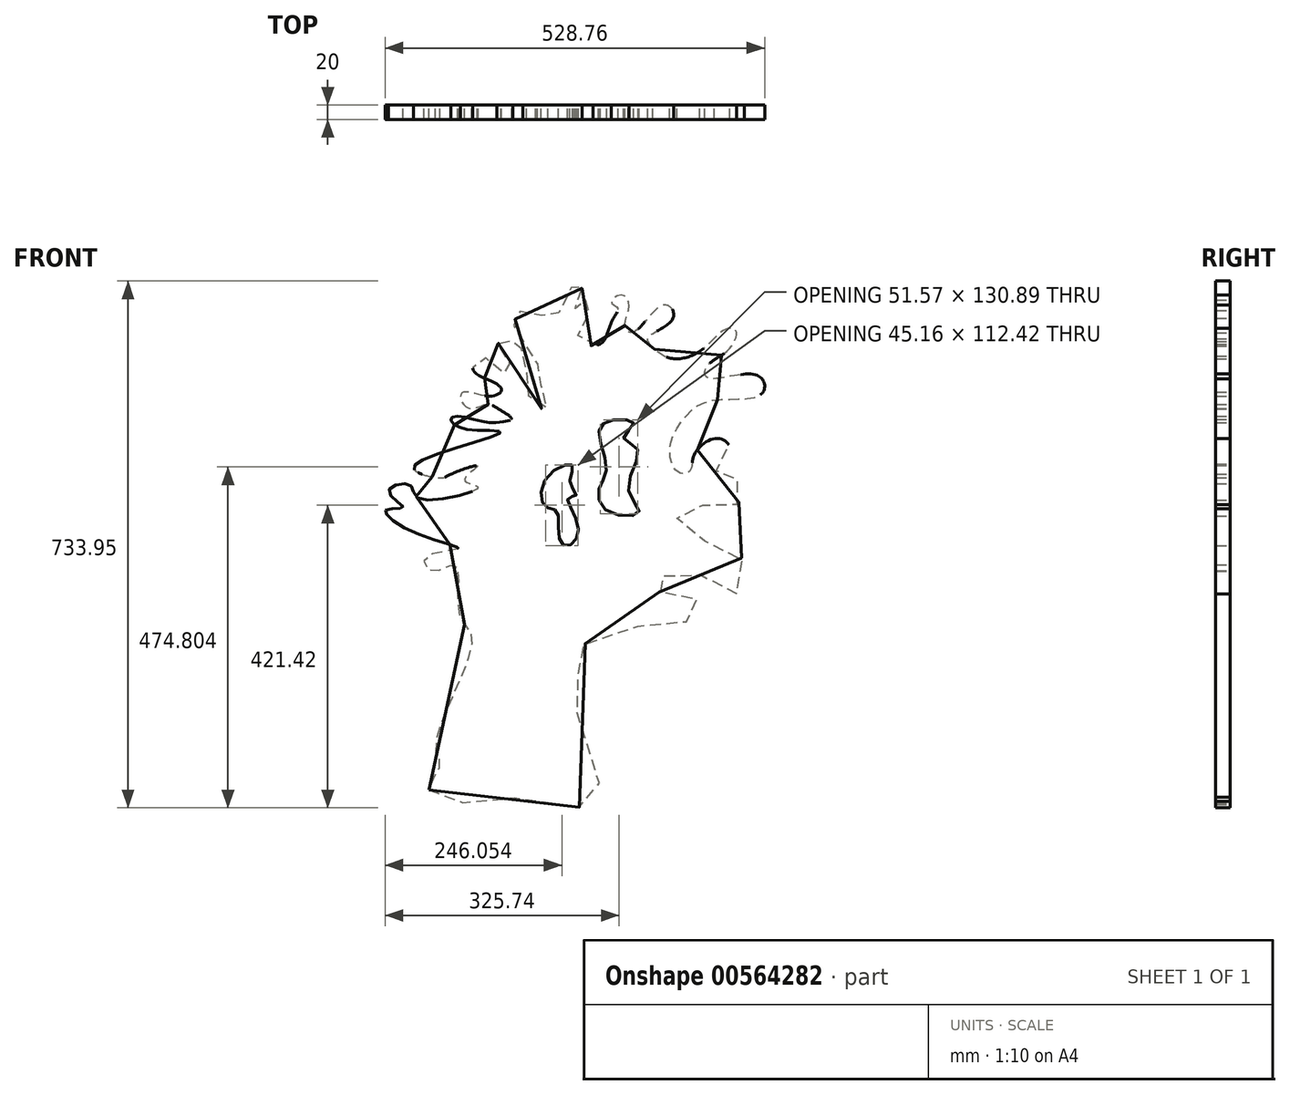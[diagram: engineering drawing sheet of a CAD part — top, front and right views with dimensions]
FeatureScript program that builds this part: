
annotation { "Feature Type Name" : "Feature", "Feature Type Description" : "" }
export const myFeature = defineFeature(function(context is Context, id is Id, definition is map)
    precondition{}
    {
        {
            var Q0;
            Q0=qCreatedBy(makeId("Front.planeOp"),FACE);
            var sketch = newSketch(context, id + "F0", { "sketchPlane" : qUnion([Q0])});
            skFitSpline(sketch, "E0", {"points": [v(-90.6, -82.86) * mm, v(-59.63, -101.05) * mm, v(20.9, -93.31) * mm, v(80.92, -103) * mm, v(91.76, -98.73) * mm, v(114.6, -106.09) * mm, v(146.74, -97.18) * mm, v(113.83, 36.4) * mm, v(117.7, 73.95) * mm, v(111.9, 103) * mm, v(175.78, 141.32) * mm, v(261.07, 149.7) * mm, v(285.07, 165.95) * mm, v(278.88, 186.09) * mm, v(232.41, 192.28) * mm, v(220.8, 200.8) * mm, v(243.26, 218.61) * mm, v(289.72, 215.51) * mm, v(335.4, 189.96) * mm, v(349.34, 218.61) * mm, v(329.98, 254.23) * mm, v(264.16, 273.6) * mm, v(257.2, 303.8) * mm, v(284.3, 314.63) * mm, v(326.89, 309.21) * mm, v(347.8, 329.35) * mm, v(340.82, 348.7) * mm, v(307.53, 353.35) * mm, v(316.82, 371.16) * mm, v(328.44, 394.4) * mm, v(309.08, 406.78) * mm, v(278.1, 382) * mm, v(273.46, 361.87) * mm, v(257.2, 358.77) * mm, v(244.8, 388.97) * mm, v(258.74, 426.91) * mm, v(292.04, 456.34) * mm, v(345.47, 461.76) * mm, v(375.67, 472.6) * mm, v(365.6, 495.06) * mm, v(297.46, 491.19) * mm, v(296.69, 507.45) * mm, v(326.89, 530.68) * mm, v(336.95, 557) * mm, v(322.24, 558.56) * mm, v(292.04, 532.23) * mm, v(261.84, 518.29) * mm, v(238.6, 520.61) * mm, v(220.8, 533.78) * mm, v(214.6, 546.94) * mm, v(244.8, 567.85) * mm, v(248.68, 585.66) * mm, v(233.19, 591.85) * mm, v(196.02, 555.46) * mm, v(185.18, 557) * mm, v(182.85, 571.72) * mm, v(188.28, 592.63) * mm, v(177.43, 606.57) * mm, v(163.5, 596.5) * mm, v(172.01, 588.76) * mm, v(164.27, 570.17) * mm, v(150.33, 539.97) * mm, v(129.42, 537.65) * mm, v(116.26, 553.14) * mm, v(129.42, 577.14) * mm, v(137.17, 596.5) * mm, v(127.1, 598.82) * mm, v(117.8, 585.66) * mm, v(113.16, 586.43) * mm, v(118.58, 605.8) * mm, v(122.45, 621.28) * mm, v(115.49, 625.93) * mm, v(100.77, 601.15) * mm, v(86.83, 578.7) * mm, v(70.57, 574.82) * mm, v(61.28, 581.79) * mm, v(36.5, 584.11) * mm, v(33.4, 578.7) * mm, v(26.43, 566.3) * mm, v(38.82, 553.91) * mm, v(41.15, 539.2) * mm, v(59.73, 512.87) * mm, v(58.18, 495.06) * mm, v(71.35, 471.05) * mm, v(72.9, 449.37) * mm, v(56.63, 453.24) * mm, v(45.02, 479.57) * mm, v(45.02, 504.35) * mm, v(38.82, 526.03) * mm, v(34.18, 543.07) * mm, v(25.66, 544.62) * mm, v(23.34, 538.42) * mm, v(8.62, 541.52) * mm, v(6.3, 522.94) * mm, v(24.88, 508.22) * mm, v(22.56, 498.16) * mm, v(7.07, 500.48) * mm, v(-10.74, 518.29) * mm, v(-22.35, 519.84) * mm, v(-29.32, 502.03) * mm, v(0, 485) * mm, v(10.17, 473.38) * mm, v(0, 466.4) * mm, v(-21.58, 467.96) * mm, v(-42.49, 471.05) * mm, v(-47.13, 463.31) * mm, v(-33.2, 448.6) * mm, v(-10.74, 454.02) * mm, v(10.95, 444.73) * mm, v(24.88, 433.88) * mm, v(11.72, 430.01) * mm, v(-8.41, 429.24) * mm, v(-36.3, 435.43) * mm, v(-57.2, 436.98) * mm, v(-60.3, 432.34) * mm, v(-53.33, 424.6) * mm, v(-26.22, 418.4) * mm, v(9.4, 415.3) * mm, v(-85.85, 382.78) * mm, v(-111.4, 363.42) * mm, v(-75, 351.8) * mm, v(-57.97, 358) * mm, v(-23.13, 368.06) * mm, v(-40.94, 348.7) * mm, v(-22.35, 338.64) * mm, v(-104.43, 323.15) * mm, v(-118.37, 342.5) * mm, v(-147.02, 333.22) * mm, v(-126.9, 310.76) * mm, v(-150.12, 307.66) * mm, v(-115.28, 277.46) * mm, v(-49.45, 252.68) * mm, v(-95.92, 240.3) * mm, v(-86.62, 221.7) * mm, v(-53.33, 230.23) * mm, v(-49.66, 163.48) * mm, v(-33.09, 136.78) * mm, v(-42.3, 83.37) * mm, v(-81.9, -26.22) * mm, v(-75.45, -48.32) * mm, v(-90.6, -82.86) * mm]});
            skFitSpline(sketch, "E1", {"points": [v(108.73, 369.76) * mm, v(71.9, 350.42) * mm, v(71.9, 311.75) * mm, v(87.55, 305.3) * mm, v(92.15, 262.94) * mm, v(107.8, 259.26) * mm, v(116.1, 289.64) * mm, v(103.2, 323.72) * mm, v(114.25, 327.4) * mm, v(105.96, 344.9) * mm, v(108.73, 369.76) * mm]});
            skFitSpline(sketch, "E2", {"points": [v(166.74, 432.38) * mm, v(146.48, 417.65) * mm, v(156.61, 365.16) * mm, v(146.48, 337.53) * mm, v(157.53, 305.3) * mm, v(201.74, 303.46) * mm, v(187, 336.6) * mm, v(199.9, 391.86) * mm, v(180.56, 407.52) * mm, v(194.37, 427.78) * mm, v(166.74, 432.38) * mm]});
            skSolve(sketch);
        }
        {
            var Q0;
            Q0=makeQuery(id+"F0.imprint","IMPRINT",FACE,{"disambiguationData":[TD([[makeQuery(id+"F0.imprint","IMPRINT",EDGE,{"derivedFrom":sQuery(id+"F0.wireOp",EDGE,"E0")}),1.0]])]});
            extrude(context, id + "F1", {"entities" : qUnion([Q0]), "depth" : 20 * mm, "offsetDistance" : 25 * mm});
        }
    });
